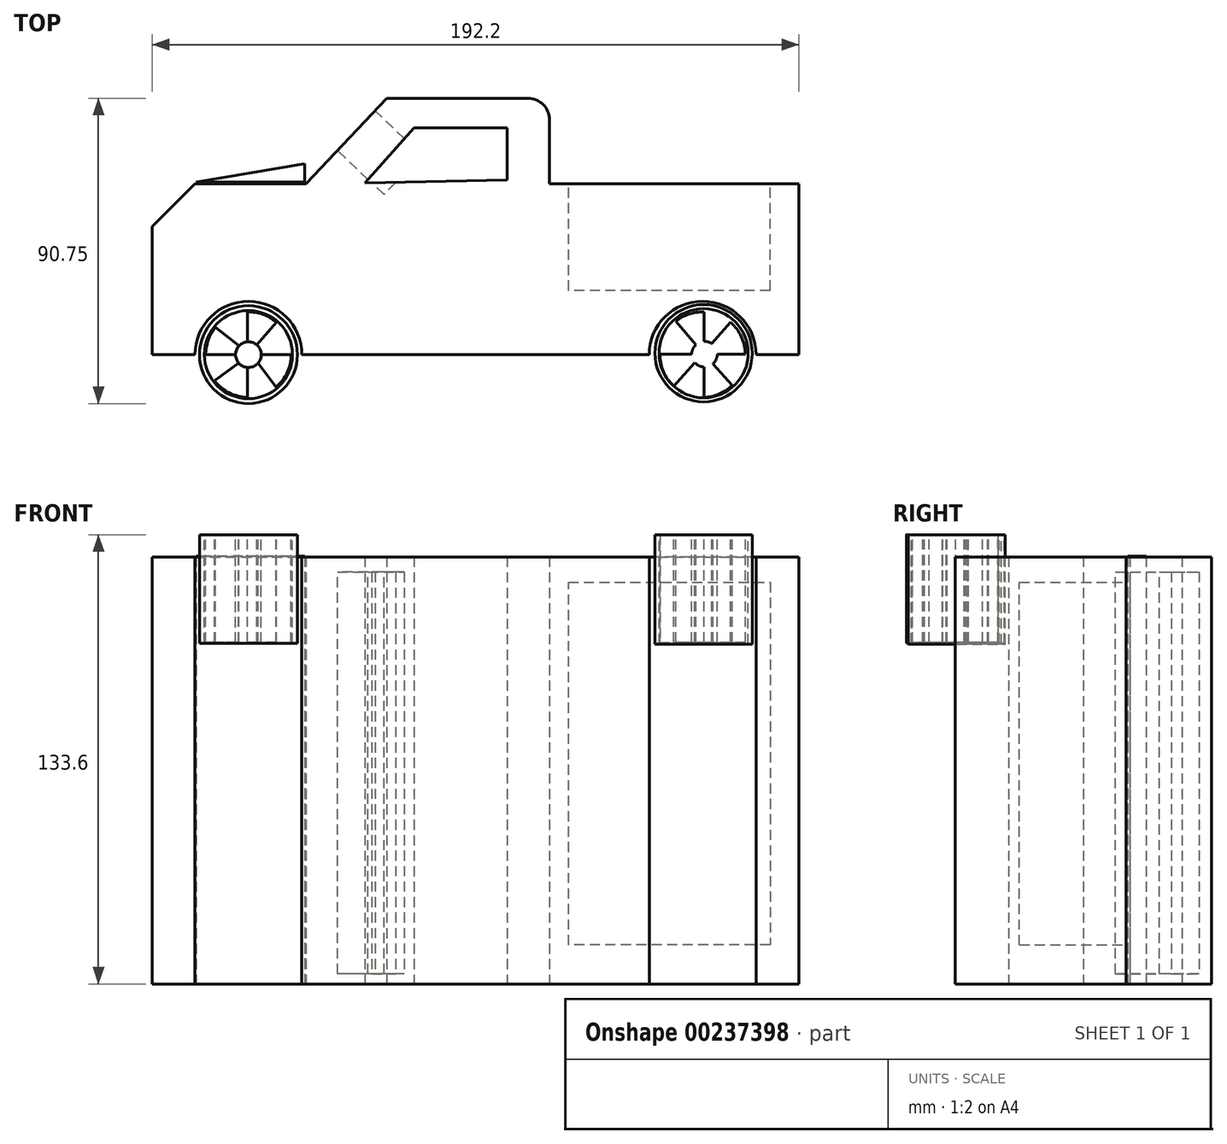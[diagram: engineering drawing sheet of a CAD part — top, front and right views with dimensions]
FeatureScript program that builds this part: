
annotation { "Feature Type Name" : "Feature", "Feature Type Description" : "" }
export const myFeature = defineFeature(function(context is Context, id is Id, definition is map)
    precondition{}
    {
        {
            var Q0;
            Q0=qCreatedBy(makeId("Top.planeOp"),FACE);
            var sketch = newSketch(context, id + "F0", { "sketchPlane" : qUnion([Q0])});
            skLineSegment(sketch, "E0", {"start": v(-98.08, -20.07) * mm, "end": v(-98.08, 30.73) * mm});
            skLineSegment(sketch, "E1", {"start": v(-98.08, 30.73) * mm, "end": v(-52.36, 30.73) * mm});
            skLineSegment(sketch, "E2", {"start": v(-52.36, 30.73) * mm, "end": v(-28.39, 56.13) * mm});
            skLineSegment(sketch, "E3", {"start": v(-28.39, 56.13) * mm, "end": v(20.03, 56.13) * mm});
            skLineSegment(sketch, "E4", {"start": v(20.03, 56.13) * mm, "end": v(20.03, 30.73) * mm});
            skLineSegment(sketch, "E5", {"start": v(20.03, 30.73) * mm, "end": v(94.12, 30.73) * mm});
            skLineSegment(sketch, "E6", {"start": v(94.12, 30.73) * mm, "end": v(94.12, -20.07) * mm});
            skLineSegment(sketch, "E7", {"start": v(94.12, -20.07) * mm, "end": v(81.42, -20.07) * mm});
            skArc(sketch, "E8", {"start": v(-53.63, -20.07) * mm, "mid": v(-69.5, -4.2) * mm, "end": v(-85.38, -20.07) * mm});
            skArc(sketch, "E9", {"start": v(81.42, -20.07) * mm, "mid": v(65.54, -4.2) * mm, "end": v(49.67, -20.07) * mm});
            skLineSegment(sketch, "E10.trimOffspring", {"start": v(-85.38, -20.07) * mm, "end": v(-98.08, -20.07) * mm});
            skLineSegment(sketch, "E11.trimOffspring", {"start": v(49.67, -20.07) * mm, "end": v(-53.63, -20.07) * mm});
            skLineSegment(sketch, "E12", {"start": v(-34.9, 30.94) * mm, "end": v(-20.27, 47.4) * mm});
            skLineSegment(sketch, "E13", {"start": v(-20.27, 47.4) * mm, "end": v(7.47, 47.4) * mm});
            skLineSegment(sketch, "E14", {"start": v(7.47, 47.4) * mm, "end": v(7.47, 31.85) * mm});
            skLineSegment(sketch, "E15", {"start": v(7.47, 31.85) * mm, "end": v(-34.9, 30.94) * mm});
            skSolve(sketch);
        }
        {
            var Q0;
            Q0 = qSketchRegion(id + "F0", true);
            extrude(context, id + "F1", {"entities" : qUnion([Q0]), "depth" : 25.4 * mm});
        }
        {
            var Q0;
            Q0=makeQuery(id+"F1.opExtrude","CAP_FACE",FACE,{"disambiguationData":[OSD([sQuery(id+"F0.wireOp",EDGE,"E0"),sQuery(id+"F0.wireOp",EDGE,"E1"),sQuery(id+"F0.wireOp",EDGE,"E2"),sQuery(id+"F0.wireOp",EDGE,"E3"),sQuery(id+"F0.wireOp",EDGE,"E4"),sQuery(id+"F0.wireOp",EDGE,"E5"),sQuery(id+"F0.wireOp",EDGE,"E6"),sQuery(id+"F0.wireOp",EDGE,"E7"),sQuery(id+"F0.wireOp",EDGE,"E8"),sQuery(id+"F0.wireOp",EDGE,"E9"),sQuery(id+"F0.wireOp",EDGE,"E10.trimOffspring"),sQuery(id+"F0.wireOp",EDGE,"E11.trimOffspring"),sQuery(id+"F0.wireOp",EDGE,"E12"),sQuery(id+"F0.wireOp",EDGE,"E13"),sQuery(id+"F0.wireOp",EDGE,"E14"),sQuery(id+"F0.wireOp",EDGE,"E15")])],"isStart":false});
            var sketch = newSketch(context, id + "F2", { "sketchPlane" : qUnion([Q0])});
            skSolve(sketch);
        }
        {
            var Q0;
            Q0=makeQuery(id+"F2.imprint","IMPRINT",FACE,{"disambiguationData":[TD([[makeQuery(id+"F2.imprint","IMPRINT",EDGE,{"derivedFrom":makeQuery(id+"F1.opExtrude","CAP_EDGE",EDGE,{"disambiguationData":[OSD([sQuery(id+"F0.wireOp",EDGE,"E0")])],"isStart":false})}),-1.0]])]});
            extrude(context, id + "F3", {"entities" : qUnion([Q0]), "depth" : 127 * mm});
        }
        {
            var Q0;
            Q0=makeQuery(id+"F3.opExtrude","SWEPT_EDGE",EDGE,{"disambiguationData":[OSD([sQuery(id+"F0.wireOp",EDGE,"E0"),sQuery(id+"F0.wireOp",EDGE,"E1")])]});
            chamfer(context, id + "F4", {"entities" : qUnion([Q0]), "width" : 12.7 * mm, "tangentPropagation" : true});
        }
        {
            var Q0;
            Q0=makeQuery(id+"F1.opExtrude","SWEPT_BODY",BODY,{"disambiguationData":[OSD([sQuery(id+"F0.wireOp",EDGE,"E0"),sQuery(id+"F0.wireOp",EDGE,"E1"),sQuery(id+"F0.wireOp",EDGE,"E2"),sQuery(id+"F0.wireOp",EDGE,"E3"),sQuery(id+"F0.wireOp",EDGE,"E4"),sQuery(id+"F0.wireOp",EDGE,"E5"),sQuery(id+"F0.wireOp",EDGE,"E6"),sQuery(id+"F0.wireOp",EDGE,"E7"),sQuery(id+"F0.wireOp",EDGE,"E8"),sQuery(id+"F0.wireOp",EDGE,"E9"),sQuery(id+"F0.wireOp",EDGE,"E10.trimOffspring"),sQuery(id+"F0.wireOp",EDGE,"E11.trimOffspring"),sQuery(id+"F0.wireOp",EDGE,"E12"),sQuery(id+"F0.wireOp",EDGE,"E13"),sQuery(id+"F0.wireOp",EDGE,"E14"),sQuery(id+"F0.wireOp",EDGE,"E15")])]});
            deleteBodies(context, id + "F5", {"entities" : qUnion([Q0])});
        }
        {
            var Q0;
            Q0=makeQuery(id+"F3.opExtrude","SWEPT_EDGE",EDGE,{"disambiguationData":[OSD([sQuery(id+"F0.wireOp",EDGE,"E3"),sQuery(id+"F0.wireOp",EDGE,"E4")])]});
            fillet(context, id + "F6", {"entities" : qUnion([Q0]), "radius" : 6.35 * mm, "tangentPropagation" : true, "allowEdgeOverflow" : false});
        }
        {
            var Q0;
            Q0=qCreatedBy(makeId("Top.planeOp"),FACE);
            var sketch = newSketch(context, id + "F7", { "sketchPlane" : qUnion([Q0])});
            skLineSegment(sketch, "E16", {"start": v(-85.04, 31.24) * mm, "end": v(-52.73, 31.24) * mm});
            skLineSegment(sketch, "E17", {"start": v(-52.73, 31.24) * mm, "end": v(-52.73, 36.73) * mm});
            skLineSegment(sketch, "E18", {"start": v(-52.73, 36.73) * mm, "end": v(-85.04, 31.24) * mm});
            skSolve(sketch);
        }
        {
            var Q0;
            Q0 = qSketchRegion(id + "F7", true);
            extrude(context, id + "F8", {"entities" : qUnion([Q0]), "depth" : 152.65 * mm});
        }
        {
            var Q0;
            Q0=qCreatedBy(makeId("Top.planeOp"),FACE);
            var sketch = newSketch(context, id + "F9", { "sketchPlane" : qUnion([Q0])});
            skLineSegment(sketch, "E19", {"start": v(-84.12, 31.85) * mm, "end": v(-53.04, 37.03) * mm});
            skLineSegment(sketch, "E20", {"start": v(-53.04, 37.03) * mm, "end": v(-53.04, 30.02) * mm});
            skLineSegment(sketch, "E21", {"start": v(-53.04, 30.02) * mm, "end": v(-84.12, 31.85) * mm});
            skSolve(sketch);
        }
        {
            var Q0;
            Q0 = qSketchRegion(id + "F9", true);
            extrude(context, id + "F10", {"entities" : qUnion([Q0]), "operationType" : NewBodyOperationType.REMOVE, "depth" : 25.4 * mm});
        }
        {
            var Q0;
            Q0=qCreatedBy(makeId("Top.planeOp"),FACE);
            var sketch = newSketch(context, id + "F11", { "sketchPlane" : qUnion([Q0])});
            skLineSegment(sketch, "E22", {"start": v(-89, 44.96) * mm, "end": v(-89, 20.27) * mm});
            skLineSegment(sketch, "E23", {"start": v(-89, 20.27) * mm, "end": v(-43.28, 22.7) * mm});
            skLineSegment(sketch, "E24", {"start": v(-43.28, 22.7) * mm, "end": v(-45.11, 57.04) * mm});
            skLineSegment(sketch, "E25", {"start": v(-45.11, 57.04) * mm, "end": v(-89, 44.96) * mm});
            skSolve(sketch);
        }
        {
            var Q0;
            Q0 = qSketchRegion(id + "F11", true);
            extrude(context, id + "F12", {"entities" : qUnion([Q0]), "operationType" : NewBodyOperationType.REMOVE, "depth" : 25.4 * mm});
        }
        {
            var Q0;
            Q0=makeQuery(id+"F3.opExtrude","SWEPT_FACE",FACE,{"disambiguationData":[OSD([sQuery(id+"F0.wireOp",EDGE,"E2")])]});
            var sketch = newSketch(context, id + "F13", { "sketchPlane" : qUnion([Q0])});
            skLineSegment(sketch, "E26", {"start": v(-16.25, 147.85) * mm, "end": v(-16.25, 28.39) * mm});
            skLineSegment(sketch, "E27", {"start": v(-16.25, 28.39) * mm, "end": v(0, 28.39) * mm});
            skLineSegment(sketch, "E28", {"start": v(0, 28.39) * mm, "end": v(0, 147.85) * mm});
            skLineSegment(sketch, "E29", {"start": v(0, 147.85) * mm, "end": v(-16.25, 147.85) * mm});
            skSolve(sketch);
        }
        {
            var Q0;
            Q0 = qSketchRegion(id + "F13", true);
            extrude(context, id + "F14", {"entities" : qUnion([Q0]), "operationType" : NewBodyOperationType.REMOVE, "oppositeDirection" : true, "depth" : 19.05 * mm});
        }
        {
            var Q0;
            Q0=makeQuery(id+"F3.opExtrude","SWEPT_FACE",FACE,{"disambiguationData":[OSD([sQuery(id+"F0.wireOp",EDGE,"E5")])]});
            var sketch = newSketch(context, id + "F15", { "sketchPlane" : qUnion([Q0])});
            skLineSegment(sketch, "E30", {"start": v(-25.66, 37) * mm, "end": v(-25.66, 144.86) * mm});
            skLineSegment(sketch, "E31", {"start": v(-25.66, 144.86) * mm, "end": v(-85.6, 144.86) * mm});
            skLineSegment(sketch, "E32", {"start": v(-85.6, 144.86) * mm, "end": v(-85.6, 37) * mm});
            skLineSegment(sketch, "E33", {"start": v(-85.6, 37) * mm, "end": v(-25.66, 37) * mm});
            skSolve(sketch);
        }
        {
            var Q0;
            Q0 = qSketchRegion(id + "F15", true);
            extrude(context, id + "F16", {"entities" : qUnion([Q0]), "operationType" : NewBodyOperationType.REMOVE, "oppositeDirection" : true, "depth" : 31.75 * mm});
        }
        {
            var Q0;
            Q0=makeQuery(id+"F3.opExtrude","CAP_FACE",FACE,{"disambiguationData":[OSD([sQuery(id+"F0.wireOp",EDGE,"E0"),sQuery(id+"F0.wireOp",EDGE,"E1"),sQuery(id+"F0.wireOp",EDGE,"E2"),sQuery(id+"F0.wireOp",EDGE,"E3"),sQuery(id+"F0.wireOp",EDGE,"E4"),sQuery(id+"F0.wireOp",EDGE,"E5"),sQuery(id+"F0.wireOp",EDGE,"E6"),sQuery(id+"F0.wireOp",EDGE,"E7"),sQuery(id+"F0.wireOp",EDGE,"E8"),sQuery(id+"F0.wireOp",EDGE,"E9"),sQuery(id+"F0.wireOp",EDGE,"E10.trimOffspring"),sQuery(id+"F0.wireOp",EDGE,"E11.trimOffspring"),sQuery(id+"F0.wireOp",EDGE,"E12"),sQuery(id+"F0.wireOp",EDGE,"E13"),sQuery(id+"F0.wireOp",EDGE,"E14"),sQuery(id+"F0.wireOp",EDGE,"E15")])],"isStart":false});
            var sketch = newSketch(context, id + "F17", { "sketchPlane" : qUnion([Q0])});
            skCircle(sketch, "E34", {"center": v(-69.5, -20.07) * mm, "radius": 12.7 * mm});
            skCircle(sketch, "E35", {"center": v(65.54, -20.07) * mm, "radius": 12.7 * mm});
            skSolve(sketch);
        }
        {
            var Q0;
            Q0 = qSketchRegion(id + "F17", true);
            extrude(context, id + "F18", {"entities" : qUnion([Q0]), "depth" : 6.6 * mm, "hasSecondDirection" : true, "secondDirectionOppositeDirection" : true, "secondDirectionDepth" : 25.4 * mm});
        }
        {
            var Q0;
            Q0=makeQuery(id+"F18.opExtrude","CAP_FACE",FACE,{"disambiguationData":[OSD([sQuery(id+"F17.wireOp",EDGE,"E34")])],"isStart":false});
            var sketch = newSketch(context, id + "F19", { "sketchPlane" : qUnion([Q0])});
            skCircle(sketch, "E36", {"center": v(-69.5, -20.07) * mm, "radius": 3.82 * mm});
            skLineSegment(sketch, "E37", {"start": v(-65.68, -20.07) * mm, "end": v(-56.8, -20.07) * mm});
            skLineSegment(sketch, "E38", {"start": v(-69.8, -16.26) * mm, "end": v(-69.8, -7.38) * mm});
            skLineSegment(sketch, "E39", {"start": v(-73.33, -20.07) * mm, "end": v(-82.2, -20.07) * mm});
            skLineSegment(sketch, "E40", {"start": v(-69.8, -23.89) * mm, "end": v(-69.8, -32.77) * mm});
            skLineSegment(sketch, "E41", {"start": v(-66.59, -22.55) * mm, "end": v(-61.24, -29.72) * mm});
            skPoint(sketch, "E41.endSnap0", {"position": v(-61.24, -20.07) * mm});
            skLineSegment(sketch, "E42", {"start": v(-72.42, -22.55) * mm, "end": v(-79.54, -27.86) * mm});
            skLineSegment(sketch, "E43", {"start": v(-67.03, -17.16) * mm, "end": v(-61.21, -10.46) * mm});
            skLineSegment(sketch, "E44", {"start": v(-72.28, -17.45) * mm, "end": v(-79.3, -12) * mm});
            skSolve(sketch);
        }
        {
            var Q0;
            Q0 = qSketchRegion(id + "F19", true);
            var Q1;
            {var subQ0=sQuery(id+"F19.wireOp",EDGE,"E40");Q1=makeQuery(id+"F19.imprint","IMPRINT",FACE,{"disambiguationData":[TD([[makeQuery(id+"F19.imprint","IMPRINT",EDGE,{"derivedFrom":subQ0}),1.0]])]});}
            var Q2;
            {var subQ0=sQuery(id+"F19.wireOp",EDGE,"E39");Q2=makeQuery(id+"F19.imprint","IMPRINT",FACE,{"disambiguationData":[TD([[makeQuery(id+"F19.imprint","IMPRINT",EDGE,{"derivedFrom":subQ0}),1.0]])]});}
            var Q3;
            {var subQ0=sQuery(id+"F19.wireOp",EDGE,"E38");Q3=makeQuery(id+"F19.imprint","IMPRINT",FACE,{"disambiguationData":[TD([[makeQuery(id+"F19.imprint","IMPRINT",EDGE,{"derivedFrom":subQ0}),1.0]])]});}
            var Q4;
            {var subQ0=sQuery(id+"F19.wireOp",EDGE,"E37");Q4=makeQuery(id+"F19.imprint","IMPRINT",FACE,{"disambiguationData":[TD([[makeQuery(id+"F19.imprint","IMPRINT",EDGE,{"derivedFrom":subQ0}),1.0]])]});}
            extrude(context, id + "F20", {"entities" : qUnion([Q0, Q1, Q2, Q3, Q4]), "operationType" : NewBodyOperationType.REMOVE, "oppositeDirection" : true, "depth" : 42.67 * mm});
        }
        {
            var Q0;
            {var subQ0=sQuery(id+"F17.wireOp",EDGE,"E34");var subQ1=sQuery(id+"F19.wireOp",EDGE,"E38");Q0=makeQuery(id+"F20.boolean.opBoolean","SPLIT",FACE,{"disambiguationData":[TD([makeQuery(id+"F20.opExtrude","SWEPT_FACE",FACE,{"disambiguationData":[OSD([subQ1])]})])],"derivedFrom":makeQuery(id+"F18.opExtrude","CAP_FACE",FACE,{"disambiguationData":[OSD([subQ0])],"isStart":false})});}
            var sketch = newSketch(context, id + "F21", { "sketchPlane" : qUnion([Q0])});
            skCircle(sketch, "E45", {"center": v(-69.5, -20.07) * mm, "radius": 13.1 * mm});
            skCircle(sketch, "E46", {"center": v(-69.5, -20.07) * mm, "radius": 14.55 * mm});
            skSolve(sketch);
        }
        {
            var Q0;
            Q0=makeQuery(id+"F21.imprint","IMPRINT",FACE,{"disambiguationData":[TD([[makeQuery(id+"F21.imprint","IMPRINT",EDGE,{"derivedFrom":sQuery(id+"F21.wireOp",EDGE,"E45")}),-1.0]])]});
            extrude(context, id + "F22", {"entities" : qUnion([Q0]), "oppositeDirection" : true, "depth" : 32.26 * mm});
        }
        {
            var Q0;
            {var subQ0=sQuery(id+"F17.wireOp",EDGE,"E34");var subQ1=sQuery(id+"F19.wireOp",EDGE,"E37");Q0=makeQuery(id+"F20.boolean.opBoolean","SPLIT",FACE,{"disambiguationData":[TD([makeQuery(id+"F20.opExtrude","SWEPT_FACE",FACE,{"disambiguationData":[OSD([subQ1])]})])],"derivedFrom":makeQuery(id+"F18.opExtrude","CAP_FACE",FACE,{"disambiguationData":[OSD([subQ0])],"isStart":false})});}
            var sketch = newSketch(context, id + "F23", { "sketchPlane" : qUnion([Q0])});
            skCircle(sketch, "E47", {"center": v(-69.5, -20.07) * mm, "radius": 3.82 * mm});
            skSolve(sketch);
        }
        {
            var Q0;
            Q0 = qSketchRegion(id + "F23", true);
            extrude(context, id + "F24", {"entities" : qUnion([Q0]), "oppositeDirection" : true, "depth" : 32.26 * mm});
        }
        {
            var Q0;
            Q0=makeQuery(id+"F18.opExtrude","CAP_FACE",FACE,{"disambiguationData":[OSD([sQuery(id+"F17.wireOp",EDGE,"E35")])],"isStart":false});
            var sketch = newSketch(context, id + "F25", { "sketchPlane" : qUnion([Q0])});
            skLineSegment(sketch, "E48", {"start": v(65.93, -7.38) * mm, "end": v(65.93, -16.14) * mm});
            skLineSegment(sketch, "E49", {"start": v(52.84, -19.95) * mm, "end": v(62.29, -19.95) * mm});
            skLineSegment(sketch, "E50", {"start": v(57.53, -10.22) * mm, "end": v(63.58, -17.1) * mm});
            skLineSegment(sketch, "E51", {"start": v(73.84, -10.46) * mm, "end": v(68.23, -16.8) * mm});
            skCircle(sketch, "E52", {"center": v(66.1, -19.95) * mm, "radius": 3.81 * mm});
            skLineSegment(sketch, "E53.trimOffspring", {"start": v(65.93, -23.76) * mm, "end": v(65.93, -32.77) * mm});
            skLineSegment(sketch, "E54.trimOffspring", {"start": v(68.62, -22.8) * mm, "end": v(74.3, -29.26) * mm});
            skLineSegment(sketch, "E55.trimOffspring", {"start": v(69.9, -19.95) * mm, "end": v(78.24, -19.95) * mm});
            skLineSegment(sketch, "E56.trimOffspring", {"start": v(65.93, -19.4) * mm, "end": v(65.44, -19.95) * mm});
            skLineSegment(sketch, "E57.trimOffspring", {"start": v(65.93, -19.4) * mm, "end": v(65.93, -19.95) * mm});
            skLineSegment(sketch, "E58.trimOffspring", {"start": v(65.77, -19.58) * mm, "end": v(66.1, -19.95) * mm});
            skLineSegment(sketch, "E59.trimOffspring", {"start": v(63.23, -22.45) * mm, "end": v(57, -29.48) * mm});
            skLineSegment(sketch, "E60.trimOffspring", {"start": v(65.44, -19.95) * mm, "end": v(66.1, -19.95) * mm});
            skSolve(sketch);
        }
        {
            var Q0;
            {var subQ0=sQuery(id+"F25.wireOp",EDGE,"E49");Q0=makeQuery(id+"F25.imprint","IMPRINT",FACE,{"disambiguationData":[TD([[makeQuery(id+"F25.imprint","IMPRINT",EDGE,{"derivedFrom":subQ0}),1.0]])]});}
            var Q1;
            {var subQ0=sQuery(id+"F25.wireOp",EDGE,"E48");Q1=makeQuery(id+"F25.imprint","IMPRINT",FACE,{"disambiguationData":[TD([[makeQuery(id+"F25.imprint","IMPRINT",EDGE,{"derivedFrom":subQ0}),1.0]])]});}
            var Q2;
            {var subQ0=sQuery(id+"F25.wireOp",EDGE,"E54.trimOffspring");Q2=makeQuery(id+"F25.imprint","IMPRINT",FACE,{"disambiguationData":[TD([[makeQuery(id+"F25.imprint","IMPRINT",EDGE,{"derivedFrom":subQ0}),1.0]])]});}
            var Q3;
            {var subQ0=sQuery(id+"F25.wireOp",EDGE,"E53.trimOffspring");Q3=makeQuery(id+"F25.imprint","IMPRINT",FACE,{"disambiguationData":[TD([[makeQuery(id+"F25.imprint","IMPRINT",EDGE,{"derivedFrom":subQ0}),-1.0]])]});}
            extrude(context, id + "F26", {"entities" : qUnion([Q0, Q1, Q2, Q3]), "operationType" : NewBodyOperationType.REMOVE, "oppositeDirection" : true, "depth" : 37.6 * mm});
        }
        {
            var Q0;
            {var subQ0=sQuery(id+"F17.wireOp",EDGE,"E34");var subQ1=sQuery(id+"F19.wireOp",EDGE,"E38");Q0=makeQuery(id+"F20.boolean.opBoolean","SPLIT",FACE,{"disambiguationData":[TD([makeQuery(id+"F20.opExtrude","SWEPT_FACE",FACE,{"disambiguationData":[OSD([subQ1])]})])],"derivedFrom":makeQuery(id+"F18.opExtrude","CAP_FACE",FACE,{"disambiguationData":[OSD([subQ0])],"isStart":false})});}
            var sketch = newSketch(context, id + "F27", { "sketchPlane" : qUnion([Q0])});
            skCircle(sketch, "E61", {"center": v(65.84, -19.66) * mm, "radius": 13.25 * mm});
            skCircle(sketch, "E62", {"center": v(65.84, -19.66) * mm, "radius": 14.46 * mm});
            skSolve(sketch);
        }
        {
            var Q0;
            Q0=makeQuery(id+"F27.imprint","IMPRINT",FACE,{"disambiguationData":[TD([[makeQuery(id+"F27.imprint","IMPRINT",EDGE,{"derivedFrom":sQuery(id+"F27.wireOp",EDGE,"E61")}),-1.0]])]});
            extrude(context, id + "F28", {"entities" : qUnion([Q0]), "oppositeDirection" : true, "depth" : 32.5 * mm});
        }
    });
